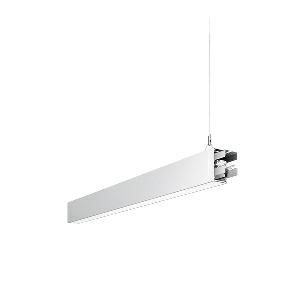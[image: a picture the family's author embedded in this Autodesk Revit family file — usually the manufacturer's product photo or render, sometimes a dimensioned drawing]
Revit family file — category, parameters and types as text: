
# Revit family: dotoo_line_-_dlp_1000_830_d_mid_00805799_fdaf
name_source: partatom
category: Lighting Fixtures
units: mm (PartAtom-declared; Revit-internal decimal feet)

## family parameters
Cut with Voids When Loaded = No
Host = Face
Light Source = No
Part Type = Normal
Room Calculation Point = No
Round Connector Dimension = Use Diameter
Shared = No

## types (1)
- DOTOO.line - DLP 1000/830/D MID (1 x LED, 1000 lm, 3000K)
    Apparent Load = 10 VA
    Approval mark = CE
    CIE Flux Codes = 67 91 98 100 100
    Color Rendering = 80-89
    Color Temperature = 3000K
    Control Gear = Electronic ballast
    Default Elevation = 1800 mm
    Description = DLP 1000/830/D|Suspended luminaire|light source: LED|connected load: 220-240 V, 50/60 Hz|Power consumption: approx. 10 W|standby: approx. 0,20|luminous flux: 1000 lm|luminous efficacy: 100 lm/W|light distribution: Direct|direct ratio: approx. 100 %|colour temperature: Warm white, ca. 3000 K|color rendering index (CRI): >= 80|chromaticity tolerance:  3 SDCM|System of protection: IP 40|technology: Continuously dimmable|luminaire body|material: Sectional aluminium|colour: White|lamp cover: Acrylic (PMMA), Clear|mains lead: 1,0 m With free stranded wires|Fastening: Steel cable 0.3 - 0.7 m|glare control: Prism aperture|luminance(L65): <= 3000 cd/m|unified glare rating(4H 8H): <=  19|special features: DALI Load 1x, TouchDIM - dimming via standard switch, Through-wired, up to 18 m on one mains connection, Flicker-free, Suitable as emergency lighting, Mechanical and electrical connection of the individual modules without tools|
    Frequency = 50 Hz
    Height = 110 mm
    Lamp = 1 x LED
    Lamp Light Flux = 1000 lm
    Lamp count = 1
    Length = 842 mm
    Luminous efficacy = 100 lm/W
    Manufacturer = Waldmann
    ModVariant = No
    Model = 00805799
    Mounting Place = Ceiling
    Mounting Type = Pendant
    Number of Poles = 1
    OnlyDefault = Yes
    Power Factor = 1
    Product Name = DOTOO.line - DLP 1000/830/D MID
    Product group = Suspended luminaire
    ProductGroupID = 9
    Protection Class = Protection class I
    Protection Degree = IP 40
    RLX_Detail_Level = 1
    RLX_Emergency_Light_Flux = 0 lm
    RLX_Emergency_Type = 0
    RLX_Emergency_Type_DB = No
    RlxData = <blob elided: 18057 chars, md5=3b76b9f3>
    Socket = socket
    Standby Power = 0 W
    System Light Flux = 1000 lm
    System Power = 10 W
    Type Comments = Product without accessories
    Type Image = 113296000-00692546.jpg
    URL = http://relux.com
    VarID = ---
    Voltage = 230 V
    Voltage Range = 220-240 V
    Weight = 0.00 kg
    Width = 60 mm  [stored 0.19685 ft]

note: [stored X ft] marks values corroborated as IEEE doubles in the binary element streams (Revit-internal decimal feet)

## geometry (parser evidence)
native form markers: Blend x4, Sweep x13
no freeform markers — native parametric forms only
